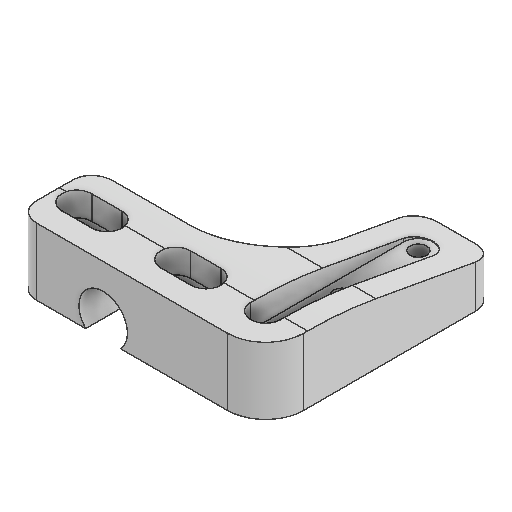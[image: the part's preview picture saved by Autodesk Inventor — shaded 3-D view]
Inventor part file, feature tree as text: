
AUTODESK INVENTOR PART (.ipt)
format: ipt  version: 2025 (Build 290162000, 162)  size: 304,640 bytes
history: native  units: in
note: dims shown in document units (in); Inventor stores cm internally (conversion verified against a paired STEP export)
features: projected_geometry x10, extrude x7, sketch x7, fillet x5, mirror x2, plane x1
ambient origin geometry x8: Origin, YZ Plane, XZ Plane, XY Plane, X Axis, Y Axis, Z Axis, Center Point
bodies: Solid1 (feature_tree)
feature tree (32):
  extrude  "Extrusion1"  Depth=0.458in
  extrude  "Extrusion2"  Depth=0.875in
  plane  "Work Plane1"
  extrude  "Extrusion3"  Depth=1.0in TaperAngle=0.0deg
  mirror  "Mirror1"
  extrude  "Extrusion4"  Depth=0.2165in
  extrude  "Extrusion5"  TaperAngle=0.0deg  [1 undecoded]
  extrude  "Extrusion6"  Depth=3.0in
  fillet  "Fillet2"  Radius=1.0in
  fillet  "Fillet3"  Radius=1.0in
  fillet  "Fillet4"  Radius=0.315in
  extrude  "Extrusion7"  Depth=5.0in
  fillet  "Fillet5"  Radius=1.0in
  fillet  "Fillet6"  Radius=0.25in
  mirror  "Mirror3"
  sketch  "Sketch1"  dims[d0=0.635in d1=0.458in]
  sketch  "Sketch2"  dims[d2=2.25in d3=0.875in]
  projected_geometry  "Projected Loop1"
  projected_geometry  "Projected Loop2"
  sketch  "Sketch3"  dims[d4=0.875in d5=1.0in d6=0.0in]
  projected_geometry  "Projected Loop3"
  sketch  "Sketch4"  dims[d7=0.2165in d8=0.2165in]
  projected_geometry  "Projected Loop4"
  sketch  "Sketch5"  dims[d9=0.3937in d10=0.0in d11=0.0in]
  projected_geometry  "Projected Loop5"
  sketch  "Sketch6"  dims[d12=0.315in d13=0.0in d15=3.0in d16=1.0in d17=1.0in d18=0.0in d19=0.315in d20=0.0in]
  projected_geometry  "Projected Loop6"
  projected_geometry  "Projected Loop7"
  projected_geometry  "Projected Loop8"
  sketch  "Sketch7"  dims[d21=0.315in d22=0.0in d23=0.5in d24=1.0in d25=0.25in d26=0.0in d27=0.0in d28=0.25in d29=5.0in]
  projected_geometry  "Projected Loop9"
  projected_geometry  "Projected Loop10"
note: 1 required parameter value undecoded (feature->parameter linkage not recoverable at this tier; creation-order binding heuristic only, values carry confidence <= 0.55)
